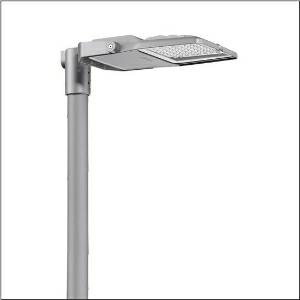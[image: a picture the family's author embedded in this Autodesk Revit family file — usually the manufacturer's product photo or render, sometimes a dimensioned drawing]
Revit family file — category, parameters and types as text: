
# Revit family: floodlight_fl_21_iq_mini___pl52_5xa7772c4d3a_40ba
name_source: partatom
category: Lighting Fixtures
units: mm (PartAtom-declared; Revit-internal decimal feet)

## family parameters
Cut with Voids When Loaded = No
Host = Face
Light Source = No
Part Type = Normal
Room Calculation Point = No
Round Connector Dimension = Use Diameter
Shared = No

## types (1)
- --- (1 x LED, 12720 lm, 87.2 W, 4000K)
    Apparent Load = 87 VA
    CIE Flux Codes = 26 60 98 100 100
    Color Rendering = 70
    Color Temperature = 4000K
    Default Elevation = 1800 mm
    Description = Floodlight FL 21 iQ mini, floodlight, primary light control with lens, of PMMA, primary optical cover: protective disc, of toughened safety glass, transparent, light distribution: PL52, light emission: direct distribution, installation type: surface-mounted, LED, High Power LED, rated luminous flux: 12.720lm, luminous efficacy: 146lm/W, light colour: 740, colour temperature: 4000K, control gear: iQ Street-Remote/DALI, control: Auto-Match, Temp-Guard, Night-Set, Smart-Wire, Desk-Remote (wireless, voltage-free reading and setting of iQ features in the workshop via application-optimized NFC function/RFID function), optimised constant luminous flux control (CLO 2.0), Light-Fading, Lumen-Switch, with terminal, 6-pole, mains connection: 220..240V, AC, 50/60Hz, start of lifetime: 87W, end of service life: 92W, reduction: 40W, luminaire housing, of diecast aluminium, powder-coated, Siteco® metallic grey (DB 702S), corrosivity category C5 mid according to DIN EN ISO 12944, suitable for swimming pools, chlorine-resistant, sealing non-destructively replaceable, please order mast flange separately, mast bracket, of steel, galvanised, powder-coated, protection rating (complete): IP66, insulation class (complete): insulation class II (safety insulation), certification: CE, ENEC, VDE, protection symbol: D, impact resistance: IK08, permissible operating ambient temperature: -40..+40°C, permissible operating ambient temperature for outdoor applications: -40..+50°C, standard: DIN EN 12944, LABS conformity tested according to VDMA 24364:2018-05, packaging unit: 1 piece

Light Distribution: PL52
    Height = 70 mm
    Lamp = 1 x LED
    Lamp Light Flux = 12720 lm
    Lamp Power = 87.2 W
    Lamp count = 1
    Length = 485 mm
    Luminous efficacy = 146 lm/W
    Manufacturer = Siteco
    ModVariant = No
    Model = 5XA7772C4D3A
    Number of Poles = 1
    OnlyDefault = Yes
    Power Factor = 1
    Product Name = Floodlight FL 21 iQ mini | PL52
    Product group = floodlight | pylon annexe
    ProductGroupID = 6200
    Protection Class = Protection class II
    Protection Degree = IP 66
    RLX_Detail_Level = 1
    RLX_Emergency_Light_Flux = 0 lm
    RLX_Emergency_Type = 0
    RLX_Emergency_Type_DB = No
    RlxData = <blob elided: 101609 chars, md5=2c492d5a>
    Socket = socket
    Standby Power = 0 W
    System Light Flux = 12720 lm
    System Power = 87 W
    Type Comments = factory setting: luminous flux: 100 % | dim-lin: 254 | 456 mA
    Type Image = l_1007125.jpg
    URL = http://relux.com
    VarID = @adj_164160
    Voltage = 0 V
    Weight = 0.00 kg
    Width = 337 mm

## geometry (parser evidence)
native form markers: Blend x4, Sweep x13
no freeform markers — native parametric forms only
